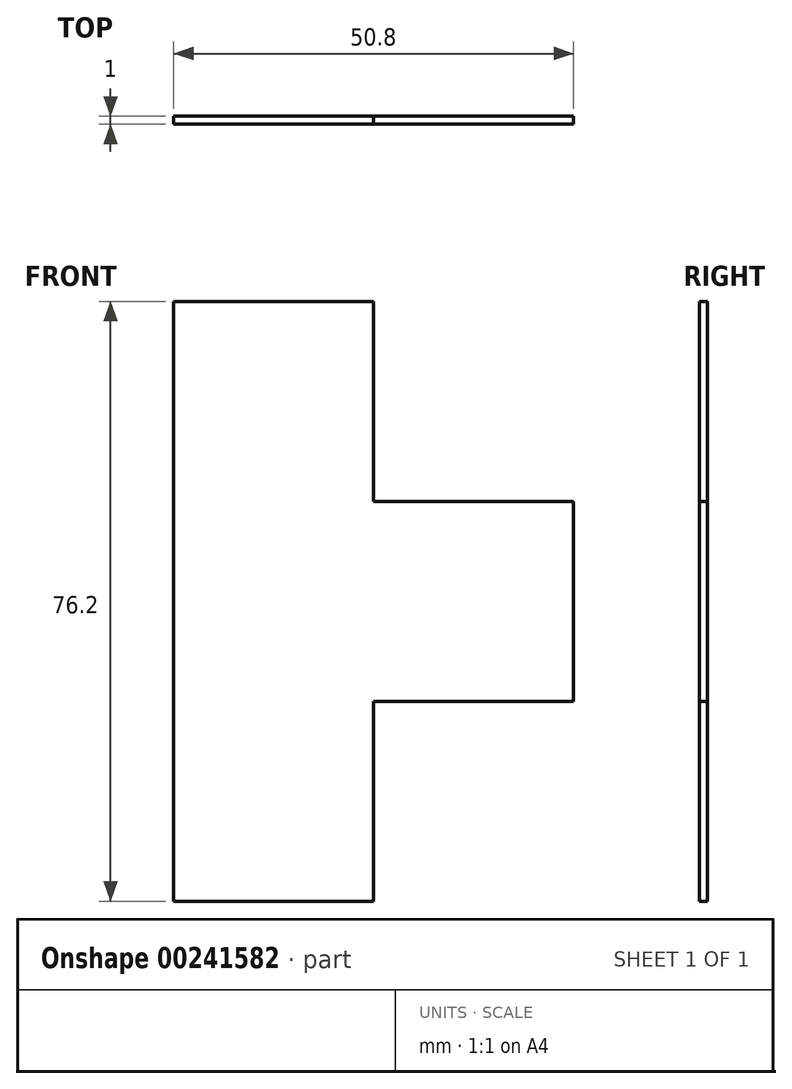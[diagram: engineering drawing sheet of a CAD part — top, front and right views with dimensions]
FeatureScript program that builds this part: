
annotation { "Feature Type Name" : "Feature", "Feature Type Description" : "" }
export const myFeature = defineFeature(function(context is Context, id is Id, definition is map)
    precondition{}
    {
        {
            assignVariable(context, id + "F0", {"name" : "x", "anyValue" : 1});
        }
        {
            var Q0;
            Q0=qCreatedBy(makeId("Front.planeOp"),FACE);
            var sketch = newSketch(context, id + "F1", { "sketchPlane" : qUnion([Q0])});
            skLineSegment(sketch, "E0.bottom", {"start": v(-25.4, 38.1) * mm, "end": v(25.4, 38.1) * mm});
            skLineSegment(sketch, "E0.top", {"start": v(-25.4, -38.1) * mm, "end": v(25.4, -38.1) * mm});
            skLineSegment(sketch, "E0.left", {"start": v(-25.4, 38.1) * mm, "end": v(-25.4, -38.1) * mm});
            skLineSegment(sketch, "E0.right", {"start": v(25.4, 38.1) * mm, "end": v(25.4, -38.1) * mm});
            skPoint(sketch, "E0.middle", {"position": v(0, 0) * mm});
            skSolve(sketch);
        }
        {
            var Q0;
            Q0=makeQuery(id+"F1.imprint","IMPRINT",FACE,{"disambiguationData":[TD([[makeQuery(id+"F1.imprint","IMPRINT",EDGE,{"derivedFrom":sQuery(id+"F1.wireOp",EDGE,"E0.bottom")}),-1.0]])]});
            extrude(context, id + "F2", {"entities" : qUnion([Q0]), "depth" : (getVariable(context, 'x')) * mm});
        }
        {
            var Q0;
            Q0=makeQuery(id+"F2.opExtrude","CAP_FACE",FACE,{"disambiguationData":[OSD([sQuery(id+"F1.wireOp",EDGE,"E0.bottom"),sQuery(id+"F1.wireOp",EDGE,"E0.top"),sQuery(id+"F1.wireOp",EDGE,"E0.left"),sQuery(id+"F1.wireOp",EDGE,"E0.right")])],"isStart":false});
            var sketch = newSketch(context, id + "F3", { "sketchPlane" : qUnion([Q0])});
            skLineSegment(sketch, "E1.bottom", {"start": v(25.4, 38.1) * mm, "end": v(0, 38.1) * mm});
            skLineSegment(sketch, "E1.top", {"start": v(25.4, 12.7) * mm, "end": v(0, 12.7) * mm});
            skLineSegment(sketch, "E1.left", {"start": v(25.4, 38.1) * mm, "end": v(25.4, 12.7) * mm});
            skLineSegment(sketch, "E1.right", {"start": v(0, 38.1) * mm, "end": v(0, 12.7) * mm});
            skSolve(sketch);
        }
        {
            var Q0;
            Q0=makeQuery(id+"F3.imprint","IMPRINT",FACE,{"disambiguationData":[TD([[makeQuery(id+"F3.imprint","IMPRINT",EDGE,{"derivedFrom":sQuery(id+"F3.wireOp",EDGE,"E1.bottom")}),-1.0]])]});
            extrude(context, id + "F4", {"entities" : qUnion([Q0]), "operationType" : NewBodyOperationType.REMOVE, "oppositeDirection" : true, "depth" : (getVariable(context, 'x')) * mm});
        }
        {
            var Q0;
            Q0=makeQuery(id+"F2.opExtrude","CAP_FACE",FACE,{"disambiguationData":[OSD([sQuery(id+"F1.wireOp",EDGE,"E0.bottom"),sQuery(id+"F1.wireOp",EDGE,"E0.top"),sQuery(id+"F1.wireOp",EDGE,"E0.left"),sQuery(id+"F1.wireOp",EDGE,"E0.right")])],"isStart":false});
            var sketch = newSketch(context, id + "F5", { "sketchPlane" : qUnion([Q0])});
            skLineSegment(sketch, "E2.bottom", {"start": v(25.4, -38.1) * mm, "end": v(0, -38.1) * mm});
            skLineSegment(sketch, "E2.top", {"start": v(25.4, -12.7) * mm, "end": v(0, -12.7) * mm});
            skLineSegment(sketch, "E2.left", {"start": v(25.4, -38.1) * mm, "end": v(25.4, -12.7) * mm});
            skLineSegment(sketch, "E2.right", {"start": v(0, -38.1) * mm, "end": v(0, -12.7) * mm});
            skSolve(sketch);
        }
        {
            var Q0;
            Q0=makeQuery(id+"F5.imprint","IMPRINT",FACE,{"disambiguationData":[TD([[makeQuery(id+"F5.imprint","IMPRINT",EDGE,{"derivedFrom":sQuery(id+"F5.wireOp",EDGE,"E2.bottom")}),1.0]])]});
            extrude(context, id + "F6", {"entities" : qUnion([Q0]), "operationType" : NewBodyOperationType.REMOVE, "oppositeDirection" : true, "depth" : (getVariable(context, 'x')) * mm});
        }
    });
